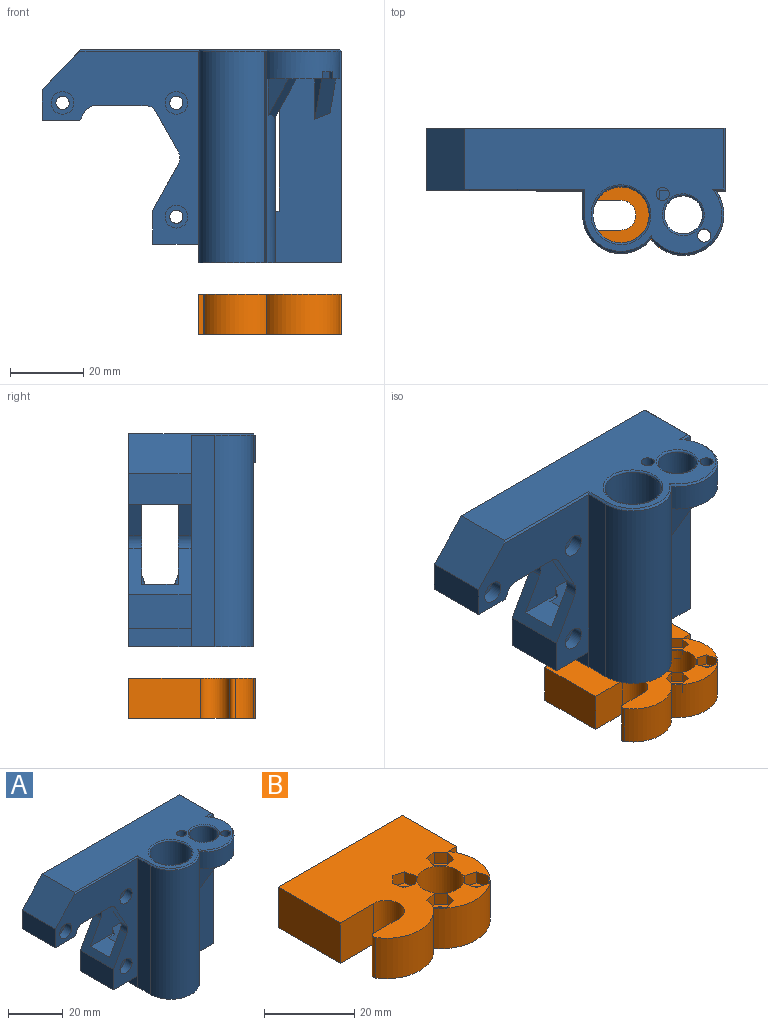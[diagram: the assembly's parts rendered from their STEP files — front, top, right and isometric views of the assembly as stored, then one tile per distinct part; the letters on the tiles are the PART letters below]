
ASSEMBLY  parts=2 mates=1
PART A: 114 faces, bbox 81.5x34.5x58 mm
  f0: cylinder r=10.47mm len=50mm, axis (0,0,1), area 313.5mm2, adj f7,f8,f32,f82,f83,f87,f105
  f1: cylinder r=7.65mm len=57.5mm, axis (0,0,1), area 2706.3mm2, adj f32,f79,f105,f106
  f2: plane 13.23x12.97mm, normal (0,0,-1), area 41.9mm2, adj f3,f4,f80,f84,f85,f86,f88,f97
  f3: plane 57.5x18.03mm, normal (0,-1,0), area 842.2mm2, adj f2,f4,f8,f17,f32,f36,f37,f38
  f4: cylinder r=11mm len=19.83mm, axis (0,0,1), area 251.4mm2, adj f2,f3,f7,f99,f100,f101,f105,f111
  f5: cylinder r=1.8mm len=6mm, axis (0,0,1), area 67.9mm2, adj f9,f101
  f6: cylinder r=1.8mm len=6mm, axis (0,0,1), area 67.9mm2, adj f9,f90
  f7: plane 15.16x13.29mm, normal (0,0,-1), area 50.2mm2, adj f0,f4,f8,f80,f82,f83,f87,f89
  f8: plane 50x6.5mm, normal (1,0,0), area 316.8mm2, adj f0,f3,f7,f32,f89,f95,f102,f103
  f9: plane 70.55x34mm, normal (0,0,1), area 1405.4mm2, adj f5,f6,f33,f41,f79,f81,f108,f109
  f10: plane 57.5x42.53mm, normal (0,-1,0), area 891.5mm2, adj f11,f23,f24,f25,f26,f28,f29,f30
  f11: cylinder r=3.5mm len=3.5mm, axis (0,1,0), area 12.4mm2, adj f10,f26,f28,f55
  f12: plane 10x3.25mm, normal (1,0,0), area 23.1mm2, adj f37,f54,f55,f58,f59,f74
  f13: plane 30.15x0.91mm, normal (0,-0.71,0.71), area 36.2mm2, adj f14,f16,f17,f70,f71
  f14: cylinder r=4.07mm len=29.1mm, axis (1,0,0), area 618.8mm2, adj f13,f15,f17,f71
  f15: plane 30.15x0.91mm, normal (0,0.71,0.71), area 36.2mm2, adj f14,f16,f17,f70,f71
  f16: plane 30.11x2.39mm, normal (0,0,1), area 70.9mm2, adj f13,f15,f17,f70
  f17: plane 57.5x17mm, normal (1,0,0), area 611.5mm2, adj f3,f13,f14,f15,f16,f32,f37,f39
  f18: plane 28x6.57mm, normal (1,0,0), area 108.5mm2, adj f37,f39,f41,f57,f58,f59
  f19: plane 28x6.57mm, normal (-1,0,0), area 108.5mm2, adj f37,f39,f41,f48,f49,f50
  f20: cylinder r=1.8mm len=13.5mm, axis (0,1,0), area 152.7mm2, adj f41,f47
  f21: cylinder r=1.8mm len=13.5mm, axis (0,1,0), area 152.7mm2, adj f41,f45
  f22: cylinder r=1.8mm len=13.5mm, axis (0,1,0), area 152.7mm2, adj f41,f43
  f23: plane 17x1.73mm, normal (0.5,0,-0.87), area 34mm2, adj f10,f24,f40,f41
  f24: plane 17x14.58mm, normal (0,0,-1), area 247.8mm2, adj f10,f23,f25,f41
  f25: cylinder r=3mm len=17mm, axis (0,1,0), area 54.2mm2, adj f10,f24,f26,f41
  f26: plane 17x11.05mm, normal (-0.87,0,-0.49), area 116.3mm2, adj f10,f11,f25,f27,f41,f55,f58,f74
  f27: cylinder r=3.5mm len=3.5mm, axis (0,1,0), area 12.4mm2, adj f26,f28,f41,f58
  f28: plane 17x12.59mm, normal (-0.87,0,0.49), area 132.8mm2, adj f10,f11,f27,f29,f41,f55,f58,f75
  f29: plane 17x9.14mm, normal (-1,0,0), area 155.4mm2, adj f10,f28,f30,f41
  f30: plane 17x12.5mm, normal (0,0,-1), area 212.5mm2, adj f10,f29,f31,f41
  f31: plane 17x5mm, normal (-1,0,0), area 85mm2, adj f10,f30,f32,f41
  f32: plane 39x33.98mm, normal (0,0,-1), area 784.9mm2, adj f0,f1,f3,f8,f10,f17,f31,f41
  f33: plane 17x10.95mm, normal (-0.72,0,0.69), area 257.1mm2, adj f9,f10,f34,f41,f108
  f34: plane 17x8.3mm, normal (-1,0,0), area 141.1mm2, adj f10,f33,f35,f41
  f35: plane 17x10.21mm, normal (0,0,-1), area 173.6mm2, adj f10,f34,f40,f41
  f36: plane 28x6.57mm, normal (1,0,0), area 108.5mm2, adj f3,f37,f39,f54,f55,f56
  f37: plane 41.5x17mm, normal (0,0,-1), area 173.3mm2, adj f3,f12,f17,f18,f19,f36,f38,f41
  f38: plane 28x6.57mm, normal (-1,0,0), area 108.5mm2, adj f3,f37,f39,f51,f52,f53
  f39: plane 41.5x17mm, normal (0,0,1), area 256.4mm2, adj f3,f17,f18,f19,f36,f38,f41,f50
  f40: plane 17x2.97mm, normal (0.87,0,-0.5), area 58.3mm2, adj f10,f23,f35,f41
  f41: plane 81.5x58mm, normal (0,1,0), area 3200.1mm2, adj f9,f17,f18,f19,f20,f21,f22,f23
  f42: cylinder r=3.1mm len=6.2mm, axis (0,-1,0), area 68.2mm2, adj f10,f43
  f43: plane 6.2x6.2mm, normal (0,-1,0), area 20mm2, adj f22,f42
  f44: cylinder r=3.1mm len=6.2mm, axis (0,-1,0), area 68.2mm2, adj f10,f45
  f45: plane 6.2x6.2mm, normal (0,-1,0), area 20mm2, adj f21,f44
  f46: cylinder r=3.1mm len=6.2mm, axis (0,-1,0), area 68.2mm2, adj f10,f47
  f47: plane 6.2x6.2mm, normal (0,-1,0), area 20mm2, adj f20,f46
  f48: plane 17x3.07mm, normal (0,-0.71,-0.71), area 73.8mm2, adj f17,f19,f37,f49
  f49: plane 19.31x17mm, normal (0,-1,0), area 328.3mm2, adj f17,f19,f48,f50
  f50: plane 17x5.62mm, normal (0,-0.94,0.34), area 101.7mm2, adj f17,f19,f39,f49
  f51: plane 17x5.62mm, normal (0,0.94,0.34), area 101.7mm2, adj f17,f38,f39,f52
  f52: plane 19.31x17mm, normal (0,1,0), area 328.3mm2, adj f17,f38,f51,f53
  f53: plane 17x3.07mm, normal (0,0.71,-0.71), area 73.8mm2, adj f17,f37,f38,f52
  f54: plane 23.5x3.07mm, normal (0,0.71,-0.71), area 102mm2, adj f12,f36,f37,f55
  f55: plane 31.95x22mm, normal (0,1,0), area 573.5mm2, adj f11,f12,f26,f28,f36,f54,f56,f73
  f56: plane 23.5x5.62mm, normal (0,0.94,0.34), area 131.9mm2, adj f36,f39,f55,f60,f73,f75
  f57: plane 23.5x5.62mm, normal (0,-0.94,0.34), area 131.9mm2, adj f18,f39,f58,f60,f75,f76
  f58: plane 31.95x22mm, normal (0,-1,0), area 573.5mm2, adj f12,f18,f26,f27,f28,f57,f59,f74
  f59: plane 23.5x3.07mm, normal (0,-0.71,-0.71), area 102mm2, adj f12,f18,f37,f58
  f60: plane 8.04x2.93mm, normal (1,0,0), area 20.4mm2, adj f39,f56,f57,f75
  f61: plane 30.15x0.91mm, normal (0,-0.71,0.71), area 36.2mm2, adj f17,f62,f64,f66,f67
  f62: cylinder r=4.07mm len=29.1mm, axis (1,0,0), area 618.8mm2, adj f17,f61,f63,f67
  f63: plane 30.15x0.91mm, normal (0,0.71,0.71), area 36.2mm2, adj f17,f62,f64,f66,f67
  f64: plane 30.11x2.39mm, normal (0,0,1), area 70.9mm2, adj f17,f61,f63,f66
  f65: cylinder r=5mm len=10mm, axis (-1,0,0), area 157.1mm2, adj f66,f68
  f66: cone r=5mm half-angle=13.6deg, axis (-1,0,0), area 85.3mm2, adj f61,f63,f64,f65,f67
  f67: plane 8.6x8.3mm, normal (-1,0,0), area 5.1mm2, adj f61,f62,f63,f66
  f68: plane 10x10mm, normal (1,0,0), area 78.5mm2, adj f65
  f69: cylinder r=5mm len=10mm, axis (1,0,0), area 157.1mm2, adj f70,f72
  f70: cone r=5mm half-angle=13.6deg, axis (-1,0,0), area 85.3mm2, adj f13,f15,f16,f69,f71
  f71: plane 8.6x8.3mm, normal (-1,0,0), area 5.1mm2, adj f13,f14,f15,f70
  f72: plane 10x10mm, normal (1,0,0), area 78.5mm2, adj f69
  f73: plane 2.69x0.98mm, normal (-1,0,0), area 1.3mm2, adj f55,f56,f75
  f74: plane 10x7.79mm, normal (0,0,-1), area 77.9mm2, adj f12,f26,f55,f58
  f75: plane 11.45x10mm, normal (0,0,1), area 90.3mm2, adj f28,f55,f56,f57,f58,f60,f73,f76
  f76: plane 2.69x0.98mm, normal (-1,0,0), area 1.3mm2, adj f57,f58,f75
  f77: plane 57.5x6.5mm, normal (-1,0,0), area 373.7mm2, adj f10,f32,f78,f113
  f78: cylinder r=10.47mm len=57.5mm, axis (0,0,1), area 1427.3mm2, adj f32,f77,f106,f112
  f79: torus R=8.15mm, axis (0,0,-1), area 38.6mm2, adj f1,f9,f107
  f80: cylinder r=5.2mm len=10.4mm, axis (0,0,1), area 223mm2, adj f2,f7,f81,f88,f89,f90,f96,f97
  f81: torus R=5.7mm, axis (0,0,-1), area 26.6mm2, adj f9,f80
  f82: plane 9.83x5.55mm, normal (-0.53,-0.85,0), area 32.2mm2, adj f0,f7,f87
  f83: plane 10.65x6.01mm, normal (0.53,0.85,0), area 37.8mm2, adj f0,f7,f87
  f84: plane 9.35x6.02mm, normal (0.97,0.26,0), area 29.1mm2, adj f2,f3,f86
  f85: plane 10.95x7.05mm, normal (-0.97,-0.26,0), area 40mm2, adj f2,f3,f86
  f86: plane 10.95x7.05mm, normal (0.22,-0.8,-0.55), area 48.8mm2, adj f2,f3,f84,f85
  f87: plane 10.65x7.67mm, normal (0.7,-0.44,-0.55), area 48.3mm2, adj f0,f7,f82,f83
  f88: plane 3x2.36mm, normal (-0.5,-0.87,0), area 5.5mm2, adj f2,f3,f80,f90,f94,f95
  f89: plane 3x2.32mm, normal (0.87,0.5,0), area 5.4mm2, adj f7,f8,f80,f90,f91,f95
  f90: plane 9.02x8.99mm, normal (0,0,-1), area 25.2mm2, adj f6,f80,f88,f89,f91,f92,f93,f94
  f91: plane 3x2.44mm, normal (0.71,0.71,0), area 10.3mm2, adj f89,f90,f92,f95
  f92: plane 3.33x3mm, normal (0.97,-0.26,0), area 10.4mm2, adj f90,f91,f93,f95
  f93: plane 3.33x3mm, normal (0.26,-0.97,0), area 10.4mm2, adj f90,f92,f94,f95
  f94: plane 3x2.44mm, normal (-0.71,-0.71,0), area 10.3mm2, adj f88,f90,f93,f95
  f95: plane 6.76x6.7mm, normal (0,0,1), area 17.2mm2, adj f3,f8,f88,f89,f91,f92,f93,f94
  f96: plane 3.36x2mm, normal (0.98,0.22,0), area 6.9mm2, adj f7,f80,f100,f101
  f97: plane 2x0.48mm, normal (0.68,-0.74,0), area 1.3mm2, adj f2,f80,f98,f101
  f98: plane 3.29x2mm, normal (-0.3,-0.95,0), area 6.9mm2, adj f2,f97,f99,f101
  f99: plane 3.14x2mm, normal (-0.98,-0.22,0), area 6.4mm2, adj f2,f4,f98,f101
  f100: plane 3.21x2mm, normal (0.3,0.95,0), area 6.7mm2, adj f4,f7,f96,f101
  f101: plane 6.71x6.53mm, normal (0,0,-1), area 20.3mm2, adj f4,f5,f80,f96,f97,f98,f99,f100
  f102: plane 4.43x3.97mm, normal (0.67,-0.74,0), area 5.9mm2, adj f3,f8,f103,f104
  f103: plane 4.43x3.97mm, normal (0,0,-1), area 8.8mm2, adj f3,f8,f102
  f104: plane 4.43x3.97mm, normal (0,0,1), area 8.8mm2, adj f3,f8,f102
  f105: plane 57.5x2.12mm, normal (-0.66,-0.75,0), area 162.7mm2, adj f0,f1,f4,f32,f107
  f106: plane 57.5x2.12mm, normal (0.66,0.75,0), area 162.7mm2, adj f1,f32,f78,f107
  f107: plane 2.78x2.62mm, normal (0,0,-1), area 2.8mm2, adj f79,f105,f106,f112
  f108: plane 33.05x0.5mm, normal (0,-0.71,0.71), area 23mm2, adj f9,f10,f33,f113
  f109: plane 17x0.5mm, normal (0.71,0,0.71), area 11.8mm2, adj f9,f17,f41,f110
  f110: plane 3.7x0.53mm, normal (0,-0.71,0.71), area 2mm2, adj f3,f9,f109,f111
  f111: cone r=10.5mm half-angle=45deg, axis (0,0,-1), area 24.4mm2, adj f4,f9,f110,f112
  f112: cone r=9.97mm half-angle=45deg, axis (0,0,-1), area 18.1mm2, adj f9,f78,f107,f111,f113
  f113: plane 7x0.5mm, normal (-0.71,0,0.71), area 4.8mm2, adj f9,f77,f108,f112
PART B: 45 faces, bbox 39x34.5x11 mm
  f0: plane 5.84x5.75mm, normal (0,0,1), area 13.2mm2, adj f15,f25,f26,f27,f28,f29,f40
  f1: plane 5.84x5.75mm, normal (0,0,1), area 13.2mm2, adj f18,f30,f31,f32,f33,f34,f41
  f2: plane 5.84x5.75mm, normal (0,0,1), area 13.2mm2, adj f14,f35,f36,f37,f38,f39,f42
  f3: plane 5.84x5.75mm, normal (0,0,1), area 13.2mm2, adj f13,f20,f21,f22,f23,f24,f43
  f4: plane 11x10.48mm, normal (0.01,-1,0), area 115.2mm2, adj f5,f17,f19,f44
  f5: cylinder r=4.05mm len=11mm, axis (0,0,1), area 140mm2, adj f4,f6,f19,f44
  f6: plane 11x8.02mm, normal (0,1,0), area 88.2mm2, adj f5,f7,f19,f44
  f7: cylinder r=1mm len=11mm, axis (0,0,1), area 23.5mm2, adj f6,f8,f19,f44
  f8: cylinder r=10.47mm len=17.03mm, axis (0,0,1), area 219.3mm2, adj f7,f9,f19,f44
  f9: cylinder r=11mm len=19.83mm, axis (0,0,1), area 379.3mm2, adj f8,f10,f19,f44
  f10: plane 11x2.65mm, normal (0,-1,0), area 29.2mm2, adj f9,f11,f19,f44
  f11: plane 17x11mm, normal (1,0,0), area 187mm2, adj f10,f12,f19,f44
  f12: plane 39x11mm, normal (0,1,0), area 429mm2, adj f11,f17,f19,f44
  f13: cylinder r=1.8mm len=8mm, axis (0,0,1), area 90.5mm2, adj f3,f19
  f14: cylinder r=1.8mm len=8mm, axis (0,0,1), area 90.5mm2, adj f2,f19
  f15: cylinder r=1.8mm len=8mm, axis (0,0,1), area 90.5mm2, adj f0,f19
  f16: cylinder r=5.25mm len=11mm, axis (0,0,1), area 362.9mm2, adj f19,f44
  f17: plane 19.54x11mm, normal (-1,0,0), area 214.9mm2, adj f4,f12,f19,f44
  f18: cylinder r=1.8mm len=8mm, axis (0,0,1), area 90.5mm2, adj f1,f19
  f19: plane 39x34.5mm, normal (0,0,-1), area 1014.1mm2, adj f4,f5,f6,f7,f8,f9,f10,f11
  f20: plane 3x2.18mm, normal (-0.73,-0.69,0), area 9mm2, adj f3,f21,f43,f44
  f21: plane 3x2.87mm, normal (-0.96,0.29,0), area 9mm2, adj f3,f20,f22,f44
  f22: plane 3x2.92mm, normal (-0.23,0.97,0), area 9mm2, adj f3,f21,f23,f44
  f23: plane 3x2.18mm, normal (0.73,0.69,0), area 9mm2, adj f3,f22,f24,f44
  f24: plane 3x2.87mm, normal (0.96,-0.29,0), area 9mm2, adj f3,f23,f43,f44
  f25: plane 3x2.18mm, normal (0.73,0.69,0), area 9mm2, adj f0,f26,f40,f44
  f26: plane 3x2.87mm, normal (0.96,-0.29,0), area 9mm2, adj f0,f25,f27,f44
  f27: plane 3x2.92mm, normal (0.23,-0.97,0), area 9mm2, adj f0,f26,f28,f44
  f28: plane 3x2.18mm, normal (-0.73,-0.69,0), area 9mm2, adj f0,f27,f29,f44
  f29: plane 3x2.87mm, normal (-0.96,0.29,0), area 9mm2, adj f0,f28,f40,f44
  f30: plane 3x2.18mm, normal (0.69,-0.73,0), area 9mm2, adj f1,f31,f41,f44
  f31: plane 3x2.87mm, normal (-0.29,-0.96,0), area 9mm2, adj f1,f30,f32,f44
  f32: plane 3x2.92mm, normal (-0.97,-0.23,0), area 9mm2, adj f1,f31,f33,f44
  f33: plane 3x2.18mm, normal (-0.69,0.73,0), area 9mm2, adj f1,f32,f34,f44
  f34: plane 3x2.87mm, normal (0.29,0.96,0), area 9mm2, adj f1,f33,f41,f44
  f35: plane 3x2.18mm, normal (-0.69,0.73,0), area 9mm2, adj f2,f36,f42,f44
  f36: plane 3x2.87mm, normal (0.29,0.96,0), area 9mm2, adj f2,f35,f37,f44
  f37: plane 3x2.92mm, normal (0.97,0.23,0), area 9mm2, adj f2,f36,f38,f44
  f38: plane 3x2.18mm, normal (0.69,-0.73,0), area 9mm2, adj f2,f37,f39,f44
  f39: plane 3x2.87mm, normal (-0.29,-0.96,0), area 9mm2, adj f2,f38,f42,f44
  f40: plane 3x2.92mm, normal (-0.23,0.97,0), area 9mm2, adj f0,f25,f29,f44
  f41: plane 3x2.92mm, normal (0.97,0.23,0), area 9mm2, adj f1,f30,f34,f44
  f42: plane 3x2.92mm, normal (-0.97,-0.23,0), area 9mm2, adj f2,f35,f39,f44
  f43: plane 3x2.92mm, normal (0.23,-0.97,0), area 9mm2, adj f3,f20,f24,f44
  f44: plane 39x34.5mm, normal (0,0,1), area 961.2mm2, adj f4,f5,f6,f7,f8,f9,f10,f11
PLACE A t=(-4.92,15.93,-2.38)mm fixed
PLACE B t=(4.5,-3.6,-46.44)mm
MATE slider A.f32 <-> B.f44  axis (0,0,-1) through (-8.38,15.93,-34.89)mm
